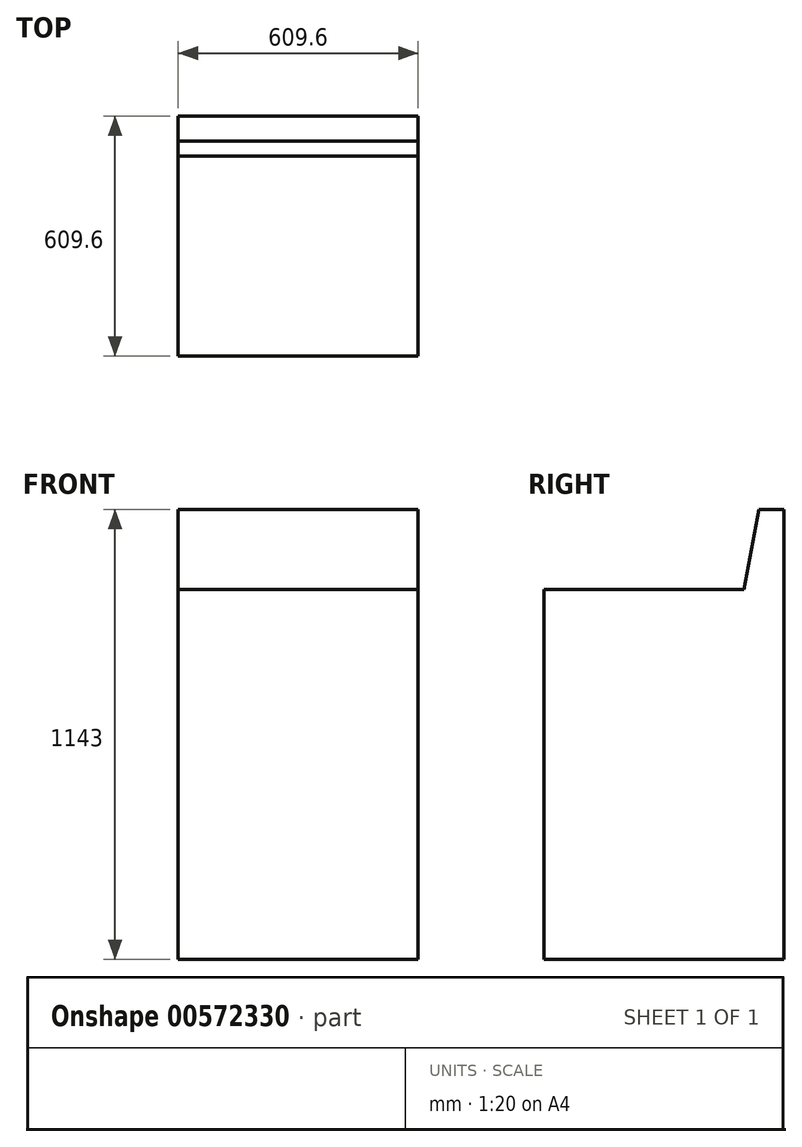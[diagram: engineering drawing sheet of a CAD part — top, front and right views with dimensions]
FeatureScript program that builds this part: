
annotation { "Feature Type Name" : "Feature", "Feature Type Description" : "" }
export const myFeature = defineFeature(function(context is Context, id is Id, definition is map)
    precondition{}
    {
        {
            var Q0;
            Q0=qCreatedBy(makeId("Right.planeOp"),FACE);
            var sketch = newSketch(context, id + "F0", { "sketchPlane" : qUnion([Q0])});
            skLineSegment(sketch, "E0.bottom", {"start": v(-436.56, -755.65) * mm, "end": v(173.04, -755.65) * mm});
            skLineSegment(sketch, "E0.top", {"start": v(-436.56, 184.15) * mm, "end": v(173.04, 184.15) * mm});
            skLineSegment(sketch, "E0.left", {"start": v(-436.56, -755.65) * mm, "end": v(-436.56, 184.15) * mm});
            skLineSegment(sketch, "E0.right", {"start": v(173.04, -755.65) * mm, "end": v(173.04, 184.15) * mm});
            skLineSegment(sketch, "E1.bottom", {"start": v(173.04, 184.15) * mm, "end": v(71.44, 184.15) * mm});
            skLineSegment(sketch, "E1.top", {"start": v(173.04, 387.35) * mm, "end": v(109.54, 387.35) * mm});
            skLineSegment(sketch, "E1.left", {"start": v(173.04, 184.15) * mm, "end": v(173.04, 387.35) * mm});
            skLineSegment(sketch, "E2", {"start": v(71.44, 184.15) * mm, "end": v(109.54, 387.35) * mm});
            skSolve(sketch);
        }
        {
            var Q0;
            Q0 = qSketchRegion(id + "F0", true);
            extrude(context, id + "F1", {"entities" : qUnion([Q0]), "depth" : 609.6 * mm, "offsetDistance" : 25.4 * mm});
        }
    });
